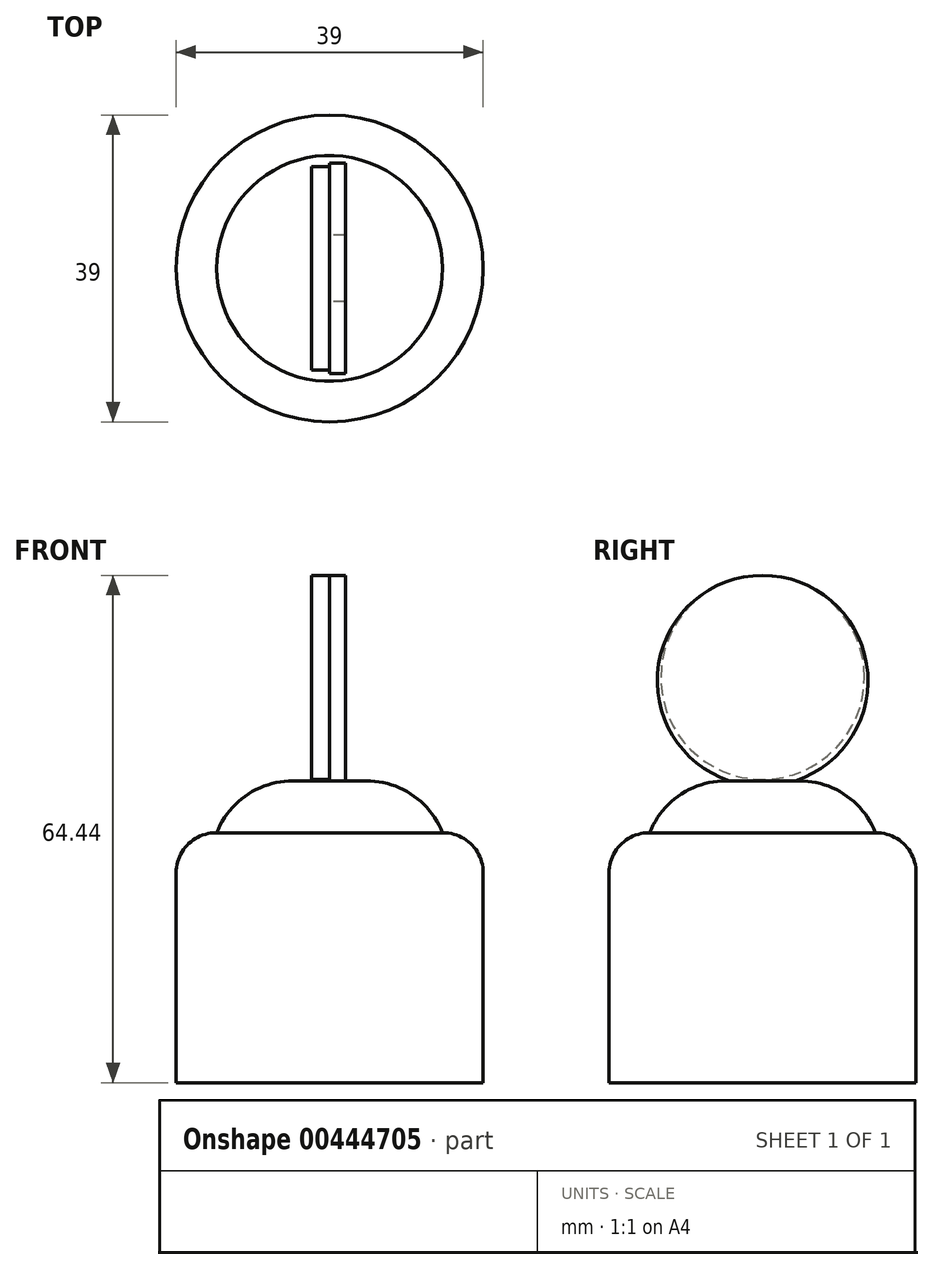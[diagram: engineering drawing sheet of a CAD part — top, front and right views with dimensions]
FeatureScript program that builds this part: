
annotation { "Feature Type Name" : "Feature", "Feature Type Description" : "" }
export const myFeature = defineFeature(function(context is Context, id is Id, definition is map)
    precondition{}
    {
        {
            var Q0;
            Q0=qCreatedBy(makeId("Top.planeOp"),FACE);
            var sketch = newSketch(context, id + "F0", { "sketchPlane" : qUnion([Q0])});
            skCircle(sketch, "E0", {"center": v(0, 0) * mm, "radius": 19.5 * mm});
            skSolve(sketch);
        }
        {
            var Q0;
            Q0=makeQuery(id+"F0.imprint","IMPRINT",FACE,{"disambiguationData":[TD([[makeQuery(id+"F0.imprint","IMPRINT",EDGE,{"derivedFrom":sQuery(id+"F0.wireOp",EDGE,"E0")}),1.0]])]});
            extrude(context, id + "F1", {"entities" : qUnion([Q0]), "depth" : 31.75 * mm});
        }
        {
            var Q0;
            Q0=makeQuery(id+"F1.opExtrude","CAP_EDGE",EDGE,{"disambiguationData":[OSD([sQuery(id+"F0.wireOp",EDGE,"E0")])],"isStart":false});
            fillet(context, id + "F2", {"entities" : qUnion([Q0]), "radius" : 5.08 * mm, "tangentPropagation" : true, "allowEdgeOverflow" : false});
        }
        {
            var Q0;
            Q0=qCreatedBy(makeId("Top.planeOp"),FACE);
            var sketch = newSketch(context, id + "F3", { "sketchPlane" : qUnion([Q0])});
            skCircle(sketch, "E1", {"center": v(0, 0) * mm, "radius": 14.35 * mm});
            skSolve(sketch);
        }
        {
            var Q0;
            Q0 = qSketchRegion(id + "F3", true);
            extrude(context, id + "F4", {"entities" : qUnion([Q0]), "operationType" : NewBodyOperationType.ADD, "depth" : 38.35 * mm});
        }
        {
            var Q0;
            Q0=makeQuery(id+"F4.opExtrude","CAP_EDGE",EDGE,{"disambiguationData":[OSD([sQuery(id+"F3.wireOp",EDGE,"E1")])],"isStart":false});
            fillet(context, id + "F5", {"entities" : qUnion([Q0]), "radius" : 10.42 * mm, "tangentPropagation" : true, "allowEdgeOverflow" : false});
        }
        {
            var Q0;
            Q0=qCreatedBy(makeId("Right.planeOp"),FACE);
            var sketch = newSketch(context, id + "F6", { "sketchPlane" : qUnion([Q0])});
            skCircle(sketch, "E2", {"center": v(0, 51.06) * mm, "radius": 13.38 * mm});
            skSolve(sketch);
        }
        {
            var Q0;
            Q0 = qSketchRegion(id + "F6", true);
            extrude(context, id + "F7", {"entities" : qUnion([Q0]), "operationType" : NewBodyOperationType.ADD, "depth" : 2.03 * mm});
        }
        {
            var Q0;
            Q0=qCreatedBy(makeId("Right.planeOp"),FACE);
            var sketch = newSketch(context, id + "F8", { "sketchPlane" : qUnion([Q0])});
            skCircle(sketch, "E3", {"center": v(0, 51.47) * mm, "radius": 12.94 * mm});
            skSolve(sketch);
        }
        {
            var Q0;
            Q0=makeQuery(id+"F8.imprint","IMPRINT",FACE,{"disambiguationData":[TD([[makeQuery(id+"F8.imprint","IMPRINT",EDGE,{"derivedFrom":sQuery(id+"F8.wireOp",EDGE,"E3")}),1.0]])]});
            extrude(context, id + "F9", {"entities" : qUnion([Q0]), "operationType" : NewBodyOperationType.ADD, "oppositeDirection" : true, "depth" : 2.3 * mm});
        }
    });
